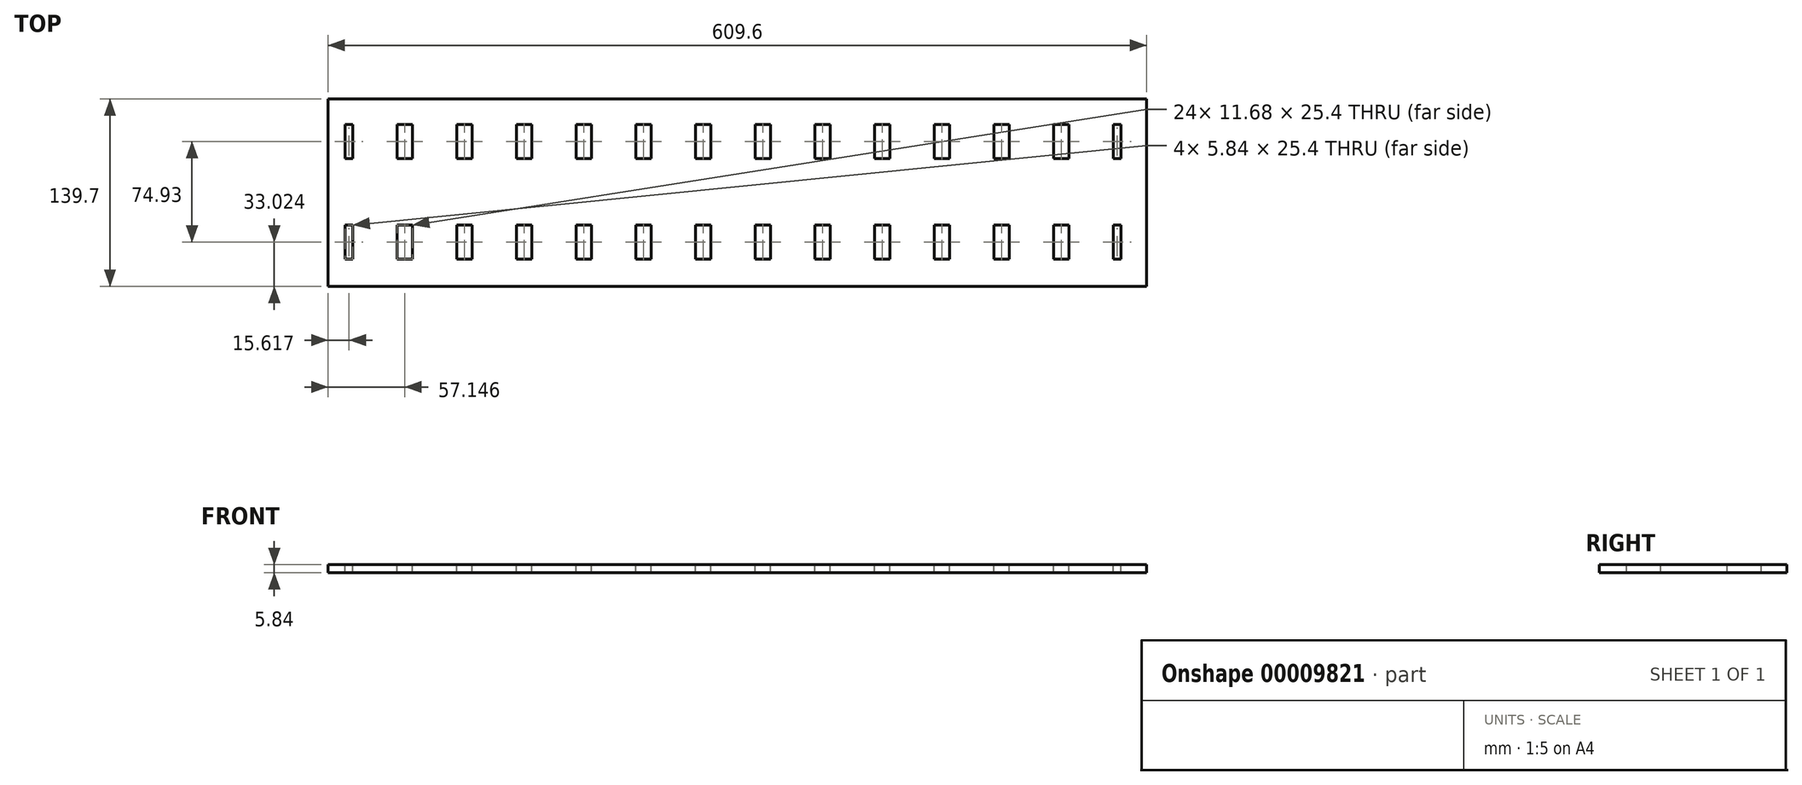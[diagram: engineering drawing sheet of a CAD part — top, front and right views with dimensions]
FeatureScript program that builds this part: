
annotation { "Feature Type Name" : "Feature", "Feature Type Description" : "" }
export const myFeature = defineFeature(function(context is Context, id is Id, definition is map)
    precondition{}
    {
        {
            var Q0;
            Q0=qCreatedBy(makeId("Top.planeOp"),FACE);
            var sketch = newSketch(context, id + "F0", { "sketchPlane" : qUnion([Q0])});
            skLineSegment(sketch, "E0.bottom", {"start": v(360.74, -82.02) * mm, "end": v(-248.86, -82.02) * mm});
            skLineSegment(sketch, "E0.top", {"start": v(360.74, 57.68) * mm, "end": v(-248.86, 57.68) * mm});
            skLineSegment(sketch, "E0.left", {"start": v(360.74, -82.02) * mm, "end": v(360.74, 57.68) * mm});
            skLineSegment(sketch, "E0.right", {"start": v(-248.86, -82.02) * mm, "end": v(-248.86, 57.68) * mm});
            skSolve(sketch);
        }
        {
            var Q0;
            Q0=makeQuery(id+"F0.imprint","IMPRINT",FACE,{"disambiguationData":[TD([[makeQuery(id+"F0.imprint","IMPRINT",EDGE,{"derivedFrom":sQuery(id+"F0.wireOp",EDGE,"E0.bottom")}),-1.0]])]});
            extrude(context, id + "F1", {"entities" : qUnion([Q0]), "oppositeDirection" : true, "depth" : 5.84 * mm});
        }
        {
            var Q0;
            Q0=makeQuery(id+"F1.opExtrude","CAP_FACE",FACE,{"disambiguationData":[OSD([sQuery(id+"F0.wireOp",EDGE,"E0.bottom"),sQuery(id+"F0.wireOp",EDGE,"E0.top"),sQuery(id+"F0.wireOp",EDGE,"E0.left"),sQuery(id+"F0.wireOp",EDGE,"E0.right")])],"isStart":true});
            var sketch = newSketch(context, id + "F2", { "sketchPlane" : qUnion([Q0])});
            skLineSegment(sketch, "E1.bottom", {"start": v(-236.16, 38.63) * mm, "end": v(-230.32, 38.63) * mm});
            skLineSegment(sketch, "E1.top", {"start": v(-236.16, 13.23) * mm, "end": v(-230.32, 13.23) * mm});
            skLineSegment(sketch, "E1.left", {"start": v(-236.16, 38.63) * mm, "end": v(-236.16, 13.23) * mm});
            skLineSegment(sketch, "E1.right", {"start": v(-230.32, 38.63) * mm, "end": v(-230.32, 13.23) * mm});
            skLineSegment(sketch, "E2.bottom", {"start": v(-236.16, -36.3) * mm, "end": v(-230.32, -36.3) * mm});
            skLineSegment(sketch, "E2.top", {"start": v(-236.16, -61.7) * mm, "end": v(-230.32, -61.7) * mm});
            skLineSegment(sketch, "E2.left", {"start": v(-236.16, -36.3) * mm, "end": v(-236.16, -61.7) * mm});
            skLineSegment(sketch, "E2.right", {"start": v(-230.32, -36.3) * mm, "end": v(-230.32, -61.7) * mm});
            skLineSegment(sketch, "E3.bottom", {"start": v(-236.16, -74.4) * mm, "end": v(-230.32, -74.4) * mm, "construction": true});
            skLineSegment(sketch, "E3.top", {"start": v(-236.16, 51.33) * mm, "end": v(-230.32, 51.33) * mm, "construction": true});
            skLineSegment(sketch, "E3.left", {"start": v(-236.16, -74.4) * mm, "end": v(-236.16, 51.33) * mm, "construction": true});
            skLineSegment(sketch, "E3.right", {"start": v(-230.32, -74.4) * mm, "end": v(-230.32, 51.33) * mm, "construction": true});
            skLineSegment(sketch, "E4.bottom", {"start": v(-197.56, 38.63) * mm, "end": v(-185.87, 38.63) * mm});
            skLineSegment(sketch, "E4.top", {"start": v(-197.56, 13.23) * mm, "end": v(-185.87, 13.23) * mm});
            skLineSegment(sketch, "E4.left", {"start": v(-197.56, 38.63) * mm, "end": v(-197.56, 13.23) * mm});
            skLineSegment(sketch, "E4.right", {"start": v(-185.87, 38.63) * mm, "end": v(-185.87, 13.23) * mm});
            skLineSegment(sketch, "E5.bottom", {"start": v(-197.56, -36.3) * mm, "end": v(-185.87, -36.3) * mm});
            skLineSegment(sketch, "E5.top", {"start": v(-197.56, -61.7) * mm, "end": v(-185.87, -61.7) * mm});
            skLineSegment(sketch, "E5.left", {"start": v(-197.56, -36.3) * mm, "end": v(-197.56, -61.7) * mm});
            skLineSegment(sketch, "E5.right", {"start": v(-185.87, -36.3) * mm, "end": v(-185.87, -61.7) * mm});
            skLineSegment(sketch, "E6.1.0.0", {"start": v(-153.1, 38.63) * mm, "end": v(-141.42, 38.63) * mm});
            skLineSegment(sketch, "E6.1.0.1", {"start": v(-153.1, 38.63) * mm, "end": v(-153.1, 13.23) * mm});
            skLineSegment(sketch, "E6.1.0.2", {"start": v(-141.42, 38.63) * mm, "end": v(-141.42, 13.23) * mm});
            skLineSegment(sketch, "E6.1.0.3", {"start": v(-153.1, 13.23) * mm, "end": v(-141.42, 13.23) * mm});
            skLineSegment(sketch, "E6.1.0.4", {"start": v(-153.1, -36.3) * mm, "end": v(-153.1, -61.7) * mm});
            skLineSegment(sketch, "E6.1.0.5", {"start": v(-153.1, -36.3) * mm, "end": v(-141.42, -36.3) * mm});
            skLineSegment(sketch, "E6.1.0.6", {"start": v(-141.42, -36.3) * mm, "end": v(-141.42, -61.7) * mm});
            skLineSegment(sketch, "E6.1.0.7", {"start": v(-153.1, -61.7) * mm, "end": v(-141.42, -61.7) * mm});
            skLineSegment(sketch, "E6.2.0.0", {"start": v(-108.66, 38.63) * mm, "end": v(-96.97, 38.63) * mm});
            skLineSegment(sketch, "E6.2.0.1", {"start": v(-108.66, 38.63) * mm, "end": v(-108.66, 13.23) * mm});
            skLineSegment(sketch, "E6.2.0.2", {"start": v(-96.97, 38.63) * mm, "end": v(-96.97, 13.23) * mm});
            skLineSegment(sketch, "E6.2.0.3", {"start": v(-108.66, 13.23) * mm, "end": v(-96.97, 13.23) * mm});
            skLineSegment(sketch, "E6.2.0.4", {"start": v(-108.66, -36.3) * mm, "end": v(-108.66, -61.7) * mm});
            skLineSegment(sketch, "E6.2.0.5", {"start": v(-108.66, -36.3) * mm, "end": v(-96.97, -36.3) * mm});
            skLineSegment(sketch, "E6.2.0.6", {"start": v(-96.97, -36.3) * mm, "end": v(-96.97, -61.7) * mm});
            skLineSegment(sketch, "E6.2.0.7", {"start": v(-108.66, -61.7) * mm, "end": v(-96.97, -61.7) * mm});
            skLineSegment(sketch, "E6.3.0.0", {"start": v(-64.2, 38.63) * mm, "end": v(-52.52, 38.63) * mm});
            skLineSegment(sketch, "E6.3.0.1", {"start": v(-64.2, 38.63) * mm, "end": v(-64.2, 13.23) * mm});
            skLineSegment(sketch, "E6.3.0.2", {"start": v(-52.52, 38.63) * mm, "end": v(-52.52, 13.23) * mm});
            skLineSegment(sketch, "E6.3.0.3", {"start": v(-64.2, 13.23) * mm, "end": v(-52.52, 13.23) * mm});
            skLineSegment(sketch, "E6.3.0.4", {"start": v(-64.2, -36.3) * mm, "end": v(-64.2, -61.7) * mm});
            skLineSegment(sketch, "E6.3.0.5", {"start": v(-64.2, -36.3) * mm, "end": v(-52.52, -36.3) * mm});
            skLineSegment(sketch, "E6.3.0.6", {"start": v(-52.52, -36.3) * mm, "end": v(-52.52, -61.7) * mm});
            skLineSegment(sketch, "E6.3.0.7", {"start": v(-64.2, -61.7) * mm, "end": v(-52.52, -61.7) * mm});
            skLineSegment(sketch, "E6.4.0.0", {"start": v(-19.76, 38.63) * mm, "end": v(-8.07, 38.63) * mm});
            skLineSegment(sketch, "E6.4.0.1", {"start": v(-19.76, 38.63) * mm, "end": v(-19.76, 13.23) * mm});
            skLineSegment(sketch, "E6.4.0.2", {"start": v(-8.07, 38.63) * mm, "end": v(-8.07, 13.23) * mm});
            skLineSegment(sketch, "E6.4.0.3", {"start": v(-19.76, 13.23) * mm, "end": v(-8.07, 13.23) * mm});
            skLineSegment(sketch, "E6.4.0.4", {"start": v(-19.76, -36.3) * mm, "end": v(-19.76, -61.7) * mm});
            skLineSegment(sketch, "E6.4.0.5", {"start": v(-19.76, -36.3) * mm, "end": v(-8.07, -36.3) * mm});
            skLineSegment(sketch, "E6.4.0.6", {"start": v(-8.07, -36.3) * mm, "end": v(-8.07, -61.7) * mm});
            skLineSegment(sketch, "E6.4.0.7", {"start": v(-19.76, -61.7) * mm, "end": v(-8.07, -61.7) * mm});
            skLineSegment(sketch, "E6.5.0.0", {"start": v(24.7, 38.63) * mm, "end": v(36.38, 38.63) * mm});
            skLineSegment(sketch, "E6.5.0.1", {"start": v(24.7, 38.63) * mm, "end": v(24.7, 13.23) * mm});
            skLineSegment(sketch, "E6.5.0.2", {"start": v(36.38, 38.63) * mm, "end": v(36.38, 13.23) * mm});
            skLineSegment(sketch, "E6.5.0.3", {"start": v(24.7, 13.23) * mm, "end": v(36.38, 13.23) * mm});
            skLineSegment(sketch, "E6.5.0.4", {"start": v(24.7, -36.3) * mm, "end": v(24.7, -61.7) * mm});
            skLineSegment(sketch, "E6.5.0.5", {"start": v(24.7, -36.3) * mm, "end": v(36.38, -36.3) * mm});
            skLineSegment(sketch, "E6.5.0.6", {"start": v(36.38, -36.3) * mm, "end": v(36.38, -61.7) * mm});
            skLineSegment(sketch, "E6.5.0.7", {"start": v(24.7, -61.7) * mm, "end": v(36.38, -61.7) * mm});
            skLineSegment(sketch, "E6.6.0.0", {"start": v(69.14, 38.63) * mm, "end": v(80.83, 38.63) * mm});
            skLineSegment(sketch, "E6.6.0.1", {"start": v(69.14, 38.63) * mm, "end": v(69.14, 13.23) * mm});
            skLineSegment(sketch, "E6.6.0.2", {"start": v(80.83, 38.63) * mm, "end": v(80.83, 13.23) * mm});
            skLineSegment(sketch, "E6.6.0.3", {"start": v(69.14, 13.23) * mm, "end": v(80.83, 13.23) * mm});
            skLineSegment(sketch, "E6.6.0.4", {"start": v(69.14, -36.3) * mm, "end": v(69.14, -61.7) * mm});
            skLineSegment(sketch, "E6.6.0.5", {"start": v(69.14, -36.3) * mm, "end": v(80.83, -36.3) * mm});
            skLineSegment(sketch, "E6.6.0.6", {"start": v(80.83, -36.3) * mm, "end": v(80.83, -61.7) * mm});
            skLineSegment(sketch, "E6.6.0.7", {"start": v(69.14, -61.7) * mm, "end": v(80.83, -61.7) * mm});
            skLineSegment(sketch, "E6.7.0.0", {"start": v(113.6, 38.63) * mm, "end": v(125.28, 38.63) * mm});
            skLineSegment(sketch, "E6.7.0.1", {"start": v(113.6, 38.63) * mm, "end": v(113.6, 13.23) * mm});
            skLineSegment(sketch, "E6.7.0.2", {"start": v(125.28, 38.63) * mm, "end": v(125.28, 13.23) * mm});
            skLineSegment(sketch, "E6.7.0.3", {"start": v(113.6, 13.23) * mm, "end": v(125.28, 13.23) * mm});
            skLineSegment(sketch, "E6.7.0.4", {"start": v(113.6, -36.3) * mm, "end": v(113.6, -61.7) * mm});
            skLineSegment(sketch, "E6.7.0.5", {"start": v(113.6, -36.3) * mm, "end": v(125.28, -36.3) * mm});
            skLineSegment(sketch, "E6.7.0.6", {"start": v(125.28, -36.3) * mm, "end": v(125.28, -61.7) * mm});
            skLineSegment(sketch, "E6.7.0.7", {"start": v(113.6, -61.7) * mm, "end": v(125.28, -61.7) * mm});
            skLineSegment(sketch, "E6.8.0.0", {"start": v(158.04, 38.63) * mm, "end": v(169.73, 38.63) * mm});
            skLineSegment(sketch, "E6.8.0.1", {"start": v(158.04, 38.63) * mm, "end": v(158.04, 13.23) * mm});
            skLineSegment(sketch, "E6.8.0.2", {"start": v(169.73, 38.63) * mm, "end": v(169.73, 13.23) * mm});
            skLineSegment(sketch, "E6.8.0.3", {"start": v(158.04, 13.23) * mm, "end": v(169.73, 13.23) * mm});
            skLineSegment(sketch, "E6.8.0.4", {"start": v(158.04, -36.3) * mm, "end": v(158.04, -61.7) * mm});
            skLineSegment(sketch, "E6.8.0.5", {"start": v(158.04, -36.3) * mm, "end": v(169.73, -36.3) * mm});
            skLineSegment(sketch, "E6.8.0.6", {"start": v(169.73, -36.3) * mm, "end": v(169.73, -61.7) * mm});
            skLineSegment(sketch, "E6.8.0.7", {"start": v(158.04, -61.7) * mm, "end": v(169.73, -61.7) * mm});
            skLineSegment(sketch, "E6.9.0.0", {"start": v(202.5, 38.63) * mm, "end": v(214.18, 38.63) * mm});
            skLineSegment(sketch, "E6.9.0.1", {"start": v(202.5, 38.63) * mm, "end": v(202.5, 13.23) * mm});
            skLineSegment(sketch, "E6.9.0.2", {"start": v(214.18, 38.63) * mm, "end": v(214.18, 13.23) * mm});
            skLineSegment(sketch, "E6.9.0.3", {"start": v(202.5, 13.23) * mm, "end": v(214.18, 13.23) * mm});
            skLineSegment(sketch, "E6.9.0.4", {"start": v(202.5, -36.3) * mm, "end": v(202.5, -61.7) * mm});
            skLineSegment(sketch, "E6.9.0.5", {"start": v(202.5, -36.3) * mm, "end": v(214.18, -36.3) * mm});
            skLineSegment(sketch, "E6.9.0.6", {"start": v(214.18, -36.3) * mm, "end": v(214.18, -61.7) * mm});
            skLineSegment(sketch, "E6.9.0.7", {"start": v(202.5, -61.7) * mm, "end": v(214.18, -61.7) * mm});
            skLineSegment(sketch, "E6.10.0.0", {"start": v(246.94, 38.63) * mm, "end": v(258.63, 38.63) * mm});
            skLineSegment(sketch, "E6.10.0.1", {"start": v(246.94, 38.63) * mm, "end": v(246.94, 13.23) * mm});
            skLineSegment(sketch, "E6.10.0.2", {"start": v(258.63, 38.63) * mm, "end": v(258.63, 13.23) * mm});
            skLineSegment(sketch, "E6.10.0.3", {"start": v(246.94, 13.23) * mm, "end": v(258.63, 13.23) * mm});
            skLineSegment(sketch, "E6.10.0.4", {"start": v(246.94, -36.3) * mm, "end": v(246.94, -61.7) * mm});
            skLineSegment(sketch, "E6.10.0.5", {"start": v(246.94, -36.3) * mm, "end": v(258.63, -36.3) * mm});
            skLineSegment(sketch, "E6.10.0.6", {"start": v(258.63, -36.3) * mm, "end": v(258.63, -61.7) * mm});
            skLineSegment(sketch, "E6.10.0.7", {"start": v(246.94, -61.7) * mm, "end": v(258.63, -61.7) * mm});
            skLineSegment(sketch, "E6.11.0.0", {"start": v(291.4, 38.63) * mm, "end": v(303.08, 38.63) * mm});
            skLineSegment(sketch, "E6.11.0.1", {"start": v(291.4, 38.63) * mm, "end": v(291.4, 13.23) * mm});
            skLineSegment(sketch, "E6.11.0.2", {"start": v(303.08, 38.63) * mm, "end": v(303.08, 13.23) * mm});
            skLineSegment(sketch, "E6.11.0.3", {"start": v(291.4, 13.23) * mm, "end": v(303.08, 13.23) * mm});
            skLineSegment(sketch, "E6.11.0.4", {"start": v(291.4, -36.3) * mm, "end": v(291.4, -61.7) * mm});
            skLineSegment(sketch, "E6.11.0.5", {"start": v(291.4, -36.3) * mm, "end": v(303.08, -36.3) * mm});
            skLineSegment(sketch, "E6.11.0.6", {"start": v(303.08, -36.3) * mm, "end": v(303.08, -61.7) * mm});
            skLineSegment(sketch, "E6.11.0.7", {"start": v(291.4, -61.7) * mm, "end": v(303.08, -61.7) * mm});
            skLineSegment(sketch, "E6.direction1", {"start": v(-197.56, 38.63) * mm, "end": v(-153.1, 38.63) * mm, "construction": true});
            skLineSegment(sketch, "E7.bottom", {"start": v(335.84, 38.63) * mm, "end": v(341.69, 38.63) * mm});
            skLineSegment(sketch, "E7.top", {"start": v(335.84, 13.23) * mm, "end": v(341.69, 13.23) * mm});
            skLineSegment(sketch, "E7.left", {"start": v(341.69, 38.63) * mm, "end": v(341.69, 13.23) * mm});
            skLineSegment(sketch, "E7.right", {"start": v(335.84, 38.63) * mm, "end": v(335.84, 13.23) * mm});
            skLineSegment(sketch, "E8.bottom", {"start": v(335.84, -36.3) * mm, "end": v(341.69, -36.3) * mm});
            skLineSegment(sketch, "E8.top", {"start": v(335.84, -61.7) * mm, "end": v(341.69, -61.7) * mm});
            skLineSegment(sketch, "E8.left", {"start": v(335.84, -36.3) * mm, "end": v(335.84, -61.7) * mm});
            skLineSegment(sketch, "E8.right", {"start": v(341.69, -36.3) * mm, "end": v(341.69, -61.7) * mm});
            skSolve(sketch);
        }
        {
            var Q0;
            Q0=makeQuery(id+"F2.imprint","IMPRINT",FACE,{"disambiguationData":[TD([[makeQuery(id+"F2.imprint","IMPRINT",EDGE,{"derivedFrom":sQuery(id+"F2.wireOp",EDGE,"E1.bottom")}),-1.0]])]});
            var Q1;
            Q1=makeQuery(id+"F2.imprint","IMPRINT",FACE,{"disambiguationData":[TD([[makeQuery(id+"F2.imprint","IMPRINT",EDGE,{"derivedFrom":sQuery(id+"F2.wireOp",EDGE,"E2.bottom")}),-1.0]])]});
            var Q2;
            Q2=makeQuery(id+"F2.imprint","IMPRINT",FACE,{"disambiguationData":[TD([[makeQuery(id+"F2.imprint","IMPRINT",EDGE,{"derivedFrom":sQuery(id+"F2.wireOp",EDGE,"E5.bottom")}),-1.0]])]});
            var Q3;
            Q3=makeQuery(id+"F2.imprint","IMPRINT",FACE,{"disambiguationData":[TD([[makeQuery(id+"F2.imprint","IMPRINT",EDGE,{"derivedFrom":sQuery(id+"F2.wireOp",EDGE,"E4.bottom")}),-1.0]])]});
            var Q4;
            Q4=makeQuery(id+"F2.imprint","IMPRINT",FACE,{"disambiguationData":[TD([[makeQuery(id+"F2.imprint","IMPRINT",EDGE,{"derivedFrom":sQuery(id+"F2.wireOp",EDGE,"E6.1.0.0")}),-1.0]])]});
            var Q5;
            Q5=makeQuery(id+"F2.imprint","IMPRINT",FACE,{"disambiguationData":[TD([[makeQuery(id+"F2.imprint","IMPRINT",EDGE,{"derivedFrom":sQuery(id+"F2.wireOp",EDGE,"E6.1.0.4")}),1.0]])]});
            var Q6;
            Q6=makeQuery(id+"F2.imprint","IMPRINT",FACE,{"disambiguationData":[TD([[makeQuery(id+"F2.imprint","IMPRINT",EDGE,{"derivedFrom":sQuery(id+"F2.wireOp",EDGE,"E6.2.0.4")}),1.0]])]});
            var Q7;
            Q7=makeQuery(id+"F2.imprint","IMPRINT",FACE,{"disambiguationData":[TD([[makeQuery(id+"F2.imprint","IMPRINT",EDGE,{"derivedFrom":sQuery(id+"F2.wireOp",EDGE,"E6.2.0.0")}),-1.0]])]});
            var Q8;
            Q8=makeQuery(id+"F2.imprint","IMPRINT",FACE,{"disambiguationData":[TD([[makeQuery(id+"F2.imprint","IMPRINT",EDGE,{"derivedFrom":sQuery(id+"F2.wireOp",EDGE,"E6.3.0.0")}),-1.0]])]});
            var Q9;
            Q9=makeQuery(id+"F2.imprint","IMPRINT",FACE,{"disambiguationData":[TD([[makeQuery(id+"F2.imprint","IMPRINT",EDGE,{"derivedFrom":sQuery(id+"F2.wireOp",EDGE,"E6.3.0.4")}),1.0]])]});
            var Q10;
            Q10=makeQuery(id+"F2.imprint","IMPRINT",FACE,{"disambiguationData":[TD([[makeQuery(id+"F2.imprint","IMPRINT",EDGE,{"derivedFrom":sQuery(id+"F2.wireOp",EDGE,"E6.4.0.4")}),1.0]])]});
            var Q11;
            Q11=makeQuery(id+"F2.imprint","IMPRINT",FACE,{"disambiguationData":[TD([[makeQuery(id+"F2.imprint","IMPRINT",EDGE,{"derivedFrom":sQuery(id+"F2.wireOp",EDGE,"E6.4.0.0")}),-1.0]])]});
            var Q12;
            Q12=makeQuery(id+"F2.imprint","IMPRINT",FACE,{"disambiguationData":[TD([[makeQuery(id+"F2.imprint","IMPRINT",EDGE,{"derivedFrom":sQuery(id+"F2.wireOp",EDGE,"E6.5.0.0")}),-1.0]])]});
            var Q13;
            Q13=makeQuery(id+"F2.imprint","IMPRINT",FACE,{"disambiguationData":[TD([[makeQuery(id+"F2.imprint","IMPRINT",EDGE,{"derivedFrom":sQuery(id+"F2.wireOp",EDGE,"E6.5.0.4")}),1.0]])]});
            var Q14;
            Q14=makeQuery(id+"F2.imprint","IMPRINT",FACE,{"disambiguationData":[TD([[makeQuery(id+"F2.imprint","IMPRINT",EDGE,{"derivedFrom":sQuery(id+"F2.wireOp",EDGE,"E6.6.0.4")}),1.0]])]});
            var Q15;
            Q15=makeQuery(id+"F2.imprint","IMPRINT",FACE,{"disambiguationData":[TD([[makeQuery(id+"F2.imprint","IMPRINT",EDGE,{"derivedFrom":sQuery(id+"F2.wireOp",EDGE,"E6.6.0.0")}),-1.0]])]});
            var Q16;
            Q16=makeQuery(id+"F2.imprint","IMPRINT",FACE,{"disambiguationData":[TD([[makeQuery(id+"F2.imprint","IMPRINT",EDGE,{"derivedFrom":sQuery(id+"F2.wireOp",EDGE,"E6.7.0.0")}),-1.0]])]});
            var Q17;
            Q17=makeQuery(id+"F2.imprint","IMPRINT",FACE,{"disambiguationData":[TD([[makeQuery(id+"F2.imprint","IMPRINT",EDGE,{"derivedFrom":sQuery(id+"F2.wireOp",EDGE,"E6.7.0.4")}),1.0]])]});
            var Q18;
            Q18=makeQuery(id+"F2.imprint","IMPRINT",FACE,{"disambiguationData":[TD([[makeQuery(id+"F2.imprint","IMPRINT",EDGE,{"derivedFrom":sQuery(id+"F2.wireOp",EDGE,"E6.8.0.4")}),1.0]])]});
            var Q19;
            Q19=makeQuery(id+"F2.imprint","IMPRINT",FACE,{"disambiguationData":[TD([[makeQuery(id+"F2.imprint","IMPRINT",EDGE,{"derivedFrom":sQuery(id+"F2.wireOp",EDGE,"E6.8.0.0")}),-1.0]])]});
            var Q20;
            Q20=makeQuery(id+"F2.imprint","IMPRINT",FACE,{"disambiguationData":[TD([[makeQuery(id+"F2.imprint","IMPRINT",EDGE,{"derivedFrom":sQuery(id+"F2.wireOp",EDGE,"E6.9.0.4")}),1.0]])]});
            var Q21;
            Q21=makeQuery(id+"F2.imprint","IMPRINT",FACE,{"disambiguationData":[TD([[makeQuery(id+"F2.imprint","IMPRINT",EDGE,{"derivedFrom":sQuery(id+"F2.wireOp",EDGE,"E6.9.0.0")}),-1.0]])]});
            var Q22;
            Q22=makeQuery(id+"F2.imprint","IMPRINT",FACE,{"disambiguationData":[TD([[makeQuery(id+"F2.imprint","IMPRINT",EDGE,{"derivedFrom":sQuery(id+"F2.wireOp",EDGE,"E6.10.0.0")}),-1.0]])]});
            var Q23;
            Q23=makeQuery(id+"F2.imprint","IMPRINT",FACE,{"disambiguationData":[TD([[makeQuery(id+"F2.imprint","IMPRINT",EDGE,{"derivedFrom":sQuery(id+"F2.wireOp",EDGE,"E6.10.0.4")}),1.0]])]});
            var Q24;
            Q24=makeQuery(id+"F2.imprint","IMPRINT",FACE,{"disambiguationData":[TD([[makeQuery(id+"F2.imprint","IMPRINT",EDGE,{"derivedFrom":sQuery(id+"F2.wireOp",EDGE,"E6.11.0.4")}),1.0]])]});
            var Q25;
            Q25=makeQuery(id+"F2.imprint","IMPRINT",FACE,{"disambiguationData":[TD([[makeQuery(id+"F2.imprint","IMPRINT",EDGE,{"derivedFrom":sQuery(id+"F2.wireOp",EDGE,"E6.11.0.0")}),-1.0]])]});
            var Q26;
            Q26=makeQuery(id+"F2.imprint","IMPRINT",FACE,{"disambiguationData":[TD([[makeQuery(id+"F2.imprint","IMPRINT",EDGE,{"derivedFrom":sQuery(id+"F2.wireOp",EDGE,"E6.12.0.0")}),-1.0]])]});
            var Q27;
            Q27=makeQuery(id+"F2.imprint","IMPRINT",FACE,{"disambiguationData":[TD([[makeQuery(id+"F2.imprint","IMPRINT",EDGE,{"derivedFrom":sQuery(id+"F2.wireOp",EDGE,"E6.12.0.4")}),1.0]])]});
            var Q28;
            Q28=makeQuery(id+"F2.imprint","IMPRINT",FACE,{"disambiguationData":[TD([[makeQuery(id+"F2.imprint","IMPRINT",EDGE,{"derivedFrom":sQuery(id+"F2.wireOp",EDGE,"E6.13.0.4")}),1.0]])]});
            var Q29;
            Q29=makeQuery(id+"F2.imprint","IMPRINT",FACE,{"disambiguationData":[TD([[makeQuery(id+"F2.imprint","IMPRINT",EDGE,{"derivedFrom":sQuery(id+"F2.wireOp",EDGE,"E6.13.0.0")}),-1.0]])]});
            var Q30;
            Q30=makeQuery(id+"F2.imprint","IMPRINT",FACE,{"disambiguationData":[TD([[makeQuery(id+"F2.imprint","IMPRINT",EDGE,{"derivedFrom":sQuery(id+"F2.wireOp",EDGE,"E6.14.0.0")}),-1.0]])]});
            var Q31;
            Q31=makeQuery(id+"F2.imprint","IMPRINT",FACE,{"disambiguationData":[TD([[makeQuery(id+"F2.imprint","IMPRINT",EDGE,{"derivedFrom":sQuery(id+"F2.wireOp",EDGE,"E6.14.0.4")}),1.0]])]});
            var Q32;
            Q32=makeQuery(id+"F2.imprint","IMPRINT",FACE,{"disambiguationData":[TD([[makeQuery(id+"F2.imprint","IMPRINT",EDGE,{"derivedFrom":sQuery(id+"F2.wireOp",EDGE,"E6.15.0.4")}),1.0]])]});
            var Q33;
            Q33=makeQuery(id+"F2.imprint","IMPRINT",FACE,{"disambiguationData":[TD([[makeQuery(id+"F2.imprint","IMPRINT",EDGE,{"derivedFrom":sQuery(id+"F2.wireOp",EDGE,"E6.15.0.0")}),-1.0]])]});
            var Q34;
            Q34=makeQuery(id+"F2.imprint","IMPRINT",FACE,{"disambiguationData":[TD([[makeQuery(id+"F2.imprint","IMPRINT",EDGE,{"derivedFrom":sQuery(id+"F2.wireOp",EDGE,"E6.16.0.0")}),-1.0]])]});
            var Q35;
            Q35=makeQuery(id+"F2.imprint","IMPRINT",FACE,{"disambiguationData":[TD([[makeQuery(id+"F2.imprint","IMPRINT",EDGE,{"derivedFrom":sQuery(id+"F2.wireOp",EDGE,"E6.16.0.4")}),1.0]])]});
            var Q36;
            Q36=makeQuery(id+"F2.imprint","IMPRINT",FACE,{"disambiguationData":[TD([[makeQuery(id+"F2.imprint","IMPRINT",EDGE,{"derivedFrom":sQuery(id+"F2.wireOp",EDGE,"E7.bottom")}),-1.0]])]});
            var Q37;
            Q37=makeQuery(id+"F2.imprint","IMPRINT",FACE,{"disambiguationData":[TD([[makeQuery(id+"F2.imprint","IMPRINT",EDGE,{"derivedFrom":sQuery(id+"F2.wireOp",EDGE,"E8.bottom")}),-1.0]])]});
            extrude(context, id + "F3", {"entities" : qUnion([Q0, Q1, Q2, Q3, Q4, Q5, Q6, Q7, Q8, Q9, Q10, Q11, Q12, Q13, Q14, Q15, Q16, Q17, Q18, Q19, Q20, Q21, Q22, Q23, Q24, Q25, Q26, Q27, Q28, Q29, Q30, Q31, Q32, Q33, Q34, Q35, Q36, Q37]), "operationType" : NewBodyOperationType.REMOVE, "oppositeDirection" : true, "depth" : 25.4 * mm});
        }
    });
